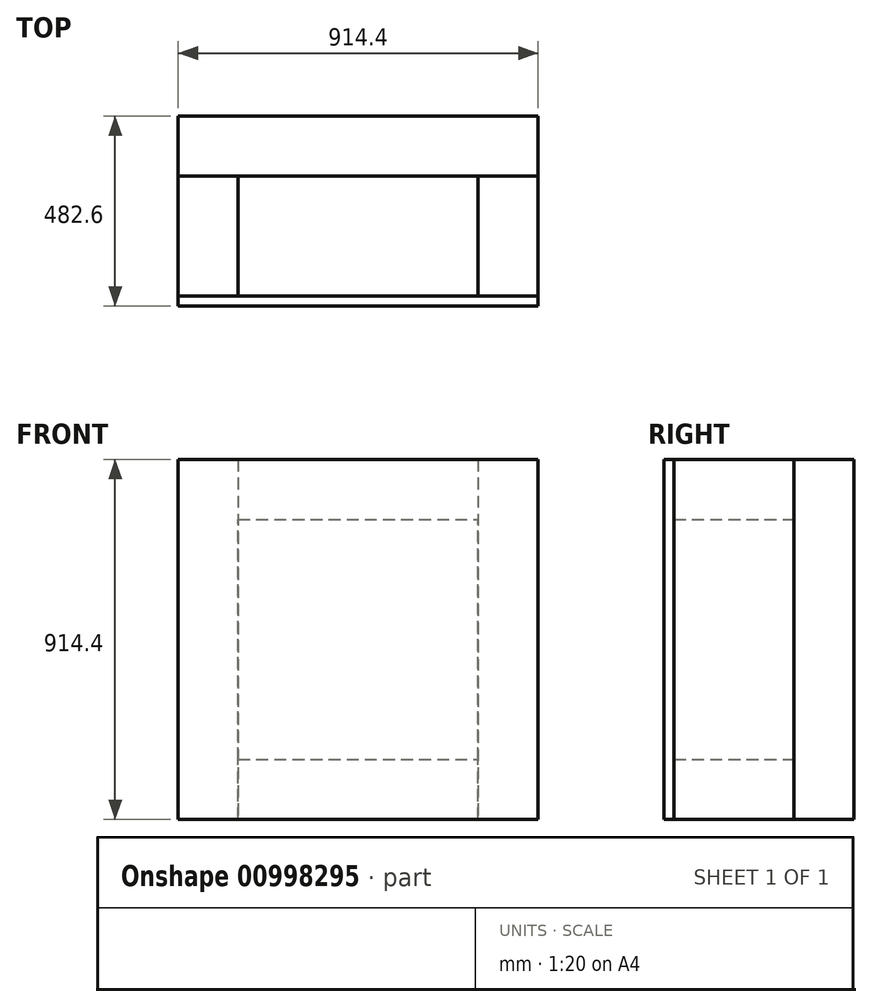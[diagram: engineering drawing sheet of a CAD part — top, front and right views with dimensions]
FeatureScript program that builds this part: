
annotation { "Feature Type Name" : "Feature", "Feature Type Description" : "" }
export const myFeature = defineFeature(function(context is Context, id is Id, definition is map)
    precondition{}
    {
        {
            var Q0;
            Q0=qCreatedBy(makeId("Front.planeOp"),FACE);
            var sketch = newSketch(context, id + "F0", { "sketchPlane" : qUnion([Q0])});
            skLineSegment(sketch, "E0.bottom", {"start": v(0, 0) * mm, "end": v(609.6, 0) * mm});
            skLineSegment(sketch, "E0.top", {"start": v(0, 609.6) * mm, "end": v(609.6, 609.6) * mm});
            skLineSegment(sketch, "E0.left", {"start": v(0, 0) * mm, "end": v(0, 609.6) * mm});
            skLineSegment(sketch, "E0.right", {"start": v(609.6, 0) * mm, "end": v(609.6, 609.6) * mm});
            skSolve(sketch);
        }
        {
            var Q0;
            Q0 = qSketchRegion(id + "F0", true);
            extrude(context, id + "F1", {"entities" : qUnion([Q0]), "depth" : 304.8 * mm, "offsetDistance" : 25.4 * mm});
        }
        {
            var Q0;
            Q0=makeQuery(id+"F1.opExtrude","SWEPT_FACE",FACE,{"disambiguationData":[OSD([sQuery(id+"F0.wireOp",EDGE,"E0.top")])]});
            var sketch = newSketch(context, id + "F2", { "sketchPlane" : qUnion([Q0])});
            skLineSegment(sketch, "E1.bottom", {"start": v(0, 0) * mm, "end": v(609.6, 0) * mm});
            skLineSegment(sketch, "E1.top", {"start": v(0, -304.8) * mm, "end": v(609.6, -304.8) * mm});
            skLineSegment(sketch, "E1.left", {"start": v(0, 0) * mm, "end": v(0, -304.8) * mm});
            skLineSegment(sketch, "E1.right", {"start": v(609.6, 0) * mm, "end": v(609.6, -304.8) * mm});
            skSolve(sketch);
        }
        {
            var Q0;
            Q0 = qSketchRegion(id + "F2", true);
            extrude(context, id + "F3", {"entities" : qUnion([Q0]), "depth" : 152.4 * mm, "offsetDistance" : 25.4 * mm});
        }
        {
            var Q0;
            Q0=makeQuery(id+"F1.opExtrude","SWEPT_FACE",FACE,{"disambiguationData":[OSD([sQuery(id+"F0.wireOp",EDGE,"E0.bottom")])]});
            var sketch = newSketch(context, id + "F4", { "sketchPlane" : qUnion([Q0])});
            skLineSegment(sketch, "E2.bottom", {"start": v(0, 0) * mm, "end": v(609.6, 0) * mm});
            skLineSegment(sketch, "E2.top", {"start": v(0, 304.8) * mm, "end": v(609.6, 304.8) * mm});
            skLineSegment(sketch, "E2.left", {"start": v(0, 0) * mm, "end": v(0, 304.8) * mm});
            skLineSegment(sketch, "E2.right", {"start": v(609.6, 0) * mm, "end": v(609.6, 304.8) * mm});
            skSolve(sketch);
        }
        {
            var Q0;
            Q0 = qSketchRegion(id + "F4", true);
            extrude(context, id + "F5", {"entities" : qUnion([Q0]), "depth" : 152.4 * mm, "offsetDistance" : 25.4 * mm});
        }
        {
            var Q0;
            Q0=makeQuery(id+"F3.opExtrude","SWEPT_FACE",FACE,{"disambiguationData":[OSD([sQuery(id+"F2.wireOp",EDGE,"E1.left")])]});
            var sketch = newSketch(context, id + "F6", { "sketchPlane" : qUnion([Q0])});
            skLineSegment(sketch, "E3.bottom", {"start": v(0, 762) * mm, "end": v(304.8, 762) * mm});
            skLineSegment(sketch, "E3.top", {"start": v(0, -152.4) * mm, "end": v(304.8, -152.4) * mm});
            skLineSegment(sketch, "E3.left", {"start": v(0, 762) * mm, "end": v(0, -152.4) * mm});
            skLineSegment(sketch, "E3.right", {"start": v(304.8, 762) * mm, "end": v(304.8, -152.4) * mm});
            skSolve(sketch);
        }
        {
            var Q0;
            Q0 = qSketchRegion(id + "F6", true);
            extrude(context, id + "F7", {"entities" : qUnion([Q0]), "depth" : 152.4 * mm, "offsetDistance" : 25.4 * mm});
        }
        {
            var Q0;
            Q0=makeQuery(id+"F3.opExtrude","SWEPT_FACE",FACE,{"disambiguationData":[OSD([sQuery(id+"F2.wireOp",EDGE,"E1.right")])]});
            var sketch = newSketch(context, id + "F8", { "sketchPlane" : qUnion([Q0])});
            skLineSegment(sketch, "E4.bottom", {"start": v(-304.8, 762) * mm, "end": v(0, 762) * mm});
            skLineSegment(sketch, "E4.top", {"start": v(-304.8, -152.4) * mm, "end": v(0, -152.4) * mm});
            skLineSegment(sketch, "E4.left", {"start": v(-304.8, 762) * mm, "end": v(-304.8, -152.4) * mm});
            skLineSegment(sketch, "E4.right", {"start": v(0, 762) * mm, "end": v(0, -152.4) * mm});
            skSolve(sketch);
        }
        {
            var Q0;
            Q0 = qSketchRegion(id + "F8", true);
            extrude(context, id + "F9", {"entities" : qUnion([Q0]), "depth" : 152.4 * mm, "offsetDistance" : 25.4 * mm});
        }
        {
            var Q0;
            Q0=makeQuery(id+"F9.opExtrude","SWEPT_FACE",FACE,{"disambiguationData":[OSD([sQuery(id+"F8.wireOp",EDGE,"E4.right")])]});
            var sketch = newSketch(context, id + "F10", { "sketchPlane" : qUnion([Q0])});
            skLineSegment(sketch, "E5.bottom", {"start": v(-762, 762) * mm, "end": v(152.4, 762) * mm});
            skLineSegment(sketch, "E5.top", {"start": v(-762, -152.4) * mm, "end": v(152.4, -152.4) * mm});
            skLineSegment(sketch, "E5.left", {"start": v(-762, 762) * mm, "end": v(-762, -152.4) * mm});
            skLineSegment(sketch, "E5.right", {"start": v(152.4, 762) * mm, "end": v(152.4, -152.4) * mm});
            skSolve(sketch);
        }
        {
            var Q0;
            Q0 = qSketchRegion(id + "F10", true);
            extrude(context, id + "F11", {"entities" : qUnion([Q0]), "depth" : 152.4 * mm, "offsetDistance" : 25.4 * mm});
        }
        {
            var Q0;
            Q0=makeQuery(id+"F7.opExtrude","SWEPT_FACE",FACE,{"disambiguationData":[OSD([sQuery(id+"F6.wireOp",EDGE,"E3.right")])]});
            var sketch = newSketch(context, id + "F12", { "sketchPlane" : qUnion([Q0])});
            skLineSegment(sketch, "E6.bottom", {"start": v(-152.4, 762) * mm, "end": v(762, 762) * mm});
            skLineSegment(sketch, "E6.top", {"start": v(-152.4, -152.4) * mm, "end": v(762, -152.4) * mm});
            skLineSegment(sketch, "E6.left", {"start": v(-152.4, 762) * mm, "end": v(-152.4, -152.4) * mm});
            skLineSegment(sketch, "E6.right", {"start": v(762, 762) * mm, "end": v(762, -152.4) * mm});
            skSolve(sketch);
        }
        {
            var Q0;
            Q0 = qSketchRegion(id + "F12", true);
            extrude(context, id + "F13", {"entities" : qUnion([Q0]), "depth" : 25.4 * mm, "offsetDistance" : 25.4 * mm});
        }
    });
